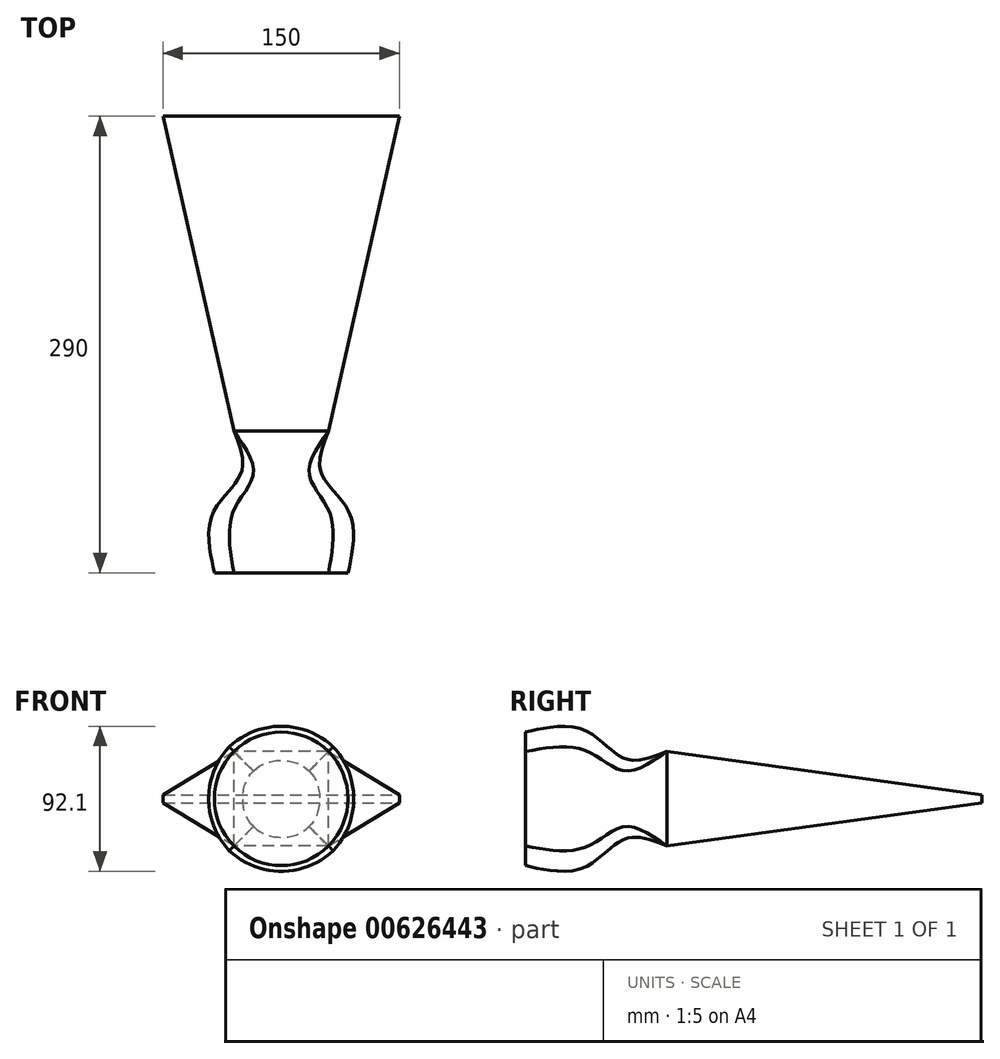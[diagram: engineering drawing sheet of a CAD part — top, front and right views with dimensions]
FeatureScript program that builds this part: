
annotation { "Feature Type Name" : "Feature", "Feature Type Description" : "" }
export const myFeature = defineFeature(function(context is Context, id is Id, definition is map)
    precondition{}
    {
        {
            var Q0;
            Q0=qCreatedBy(makeId("Front.planeOp"),FACE);
            cPlane(context, id + "F0", {"entities" : qUnion([Q0]), "cplaneType" : CPlaneType.OFFSET, "offset" : 25 * mm, "width" : 152.4 * mm, "height" : 152.4 * mm});
        }
        {
            var Q0;
            Q0=qCreatedBy(id+"F0.planeOp",FACE);
            cPlane(context, id + "F1", {"entities" : qUnion([Q0]), "cplaneType" : CPlaneType.OFFSET, "offset" : 25 * mm, "width" : 152.4 * mm, "height" : 152.4 * mm});
        }
        {
            var Q0;
            Q0=qCreatedBy(id+"F1.planeOp",FACE);
            cPlane(context, id + "F2", {"entities" : qUnion([Q0]), "cplaneType" : CPlaneType.OFFSET, "offset" : 40 * mm, "width" : 152.4 * mm, "height" : 152.4 * mm});
        }
        {
            var Q0;
            Q0=qCreatedBy(makeId("Front.planeOp"),FACE);
            var sketch = newSketch(context, id + "F3", { "sketchPlane" : qUnion([Q0])});
            skLineSegment(sketch, "E0.bottom", {"start": v(30, -30) * mm, "end": v(-30, -30) * mm});
            skLineSegment(sketch, "E0.top", {"start": v(30, 30) * mm, "end": v(-30, 30) * mm});
            skLineSegment(sketch, "E0.left", {"start": v(30, -30) * mm, "end": v(30, 30) * mm});
            skLineSegment(sketch, "E0.right", {"start": v(-30, -30) * mm, "end": v(-30, 30) * mm});
            skPoint(sketch, "E0.middle", {"position": v(0, 0) * mm});
            skSolve(sketch);
        }
        {
            var Q0;
            Q0=qCreatedBy(id+"F0.planeOp",FACE);
            var sketch = newSketch(context, id + "F4", { "sketchPlane" : qUnion([Q0])});
            skCircle(sketch, "E1", {"center": v(0, 0) * mm, "radius": 25 * mm});
            skSolve(sketch);
        }
        {
            var Q0;
            Q0=qCreatedBy(id+"F1.planeOp",FACE);
            var sketch = newSketch(context, id + "F5", { "sketchPlane" : qUnion([Q0])});
            skCircle(sketch, "E2", {"center": v(0, 0) * mm, "radius": 42.43 * mm});
            skSolve(sketch);
        }
        {
            var Q0;
            Q0=qCreatedBy(id+"F2.planeOp",FACE);
            var sketch = newSketch(context, id + "F6", { "sketchPlane" : qUnion([Q0])});
            skCircle(sketch, "E3", {"center": v(0, 0) * mm, "radius": 42.43 * mm});
            skSolve(sketch);
        }
        {
            var Q0;
            Q0 = qSketchRegion(id + "F3", true);
            var Q1;
            Q1 = qSketchRegion(id + "F4", true);
            var Q2;
            Q2 = qSketchRegion(id + "F5", true);
            var Q3;
            Q3 = qSketchRegion(id + "F6", true);
            loft(context, id + "F7", {"sheetProfilesArray" : [{ "sheetProfileEntities" : qUnion([Q0]) }, { "sheetProfileEntities" : qUnion([Q1]) }, { "sheetProfileEntities" : qUnion([Q2]) }, { "sheetProfileEntities" : qUnion([Q3]) }]});
        }
        {
            var Q0;
            Q0=qCreatedBy(makeId("Front.planeOp"),FACE);
            cPlane(context, id + "F8", {"entities" : qUnion([Q0]), "cplaneType" : CPlaneType.OFFSET, "offset" : 200 * mm, "oppositeDirection" : true, "width" : 152.4 * mm, "height" : 152.4 * mm});
        }
        {
            var Q0;
            Q0=qCreatedBy(id+"F8.planeOp",FACE);
            var sketch = newSketch(context, id + "F9", { "sketchPlane" : qUnion([Q0])});
            skLineSegment(sketch, "E4.bottom", {"start": v(-75, -2.5) * mm, "end": v(75, -2.5) * mm});
            skLineSegment(sketch, "E4.top", {"start": v(-75, 2.5) * mm, "end": v(75, 2.5) * mm});
            skLineSegment(sketch, "E4.left", {"start": v(-75, -2.5) * mm, "end": v(-75, 2.5) * mm});
            skLineSegment(sketch, "E4.right", {"start": v(75, -2.5) * mm, "end": v(75, 2.5) * mm});
            skPoint(sketch, "E4.middle", {"position": v(0, 0) * mm});
            skSolve(sketch);
        }
        {
            var Q1;
            Q1=makeQuery(id+"F7.opLoft","CAP_FACE",FACE,{"disambiguationData":[OSD([makeQuery(id+"F3.imprint","IMPRINT",FACE,{"disambiguationData":[TD([[makeQuery(id+"F3.imprint","IMPRINT",EDGE,{"derivedFrom":sQuery(id+"F3.wireOp",EDGE,"E0.bottom")}),-1.0]])]})])],"isStart":true});
            var Q2;
            Q2=makeQuery(id+"F9.imprint","IMPRINT",FACE,{"disambiguationData":[TD([[makeQuery(id+"F9.imprint","IMPRINT",EDGE,{"derivedFrom":sQuery(id+"F9.wireOp",EDGE,"E4.bottom")}),1.0]])]});
            loft(context, id + "F10", {"operationType" : NewBodyOperationType.ADD, "sheetProfilesArray" : [{ "sheetProfileEntities" : qUnion([Q1]) }, { "sheetProfileEntities" : qUnion([Q2]) }]});
        }
    });
